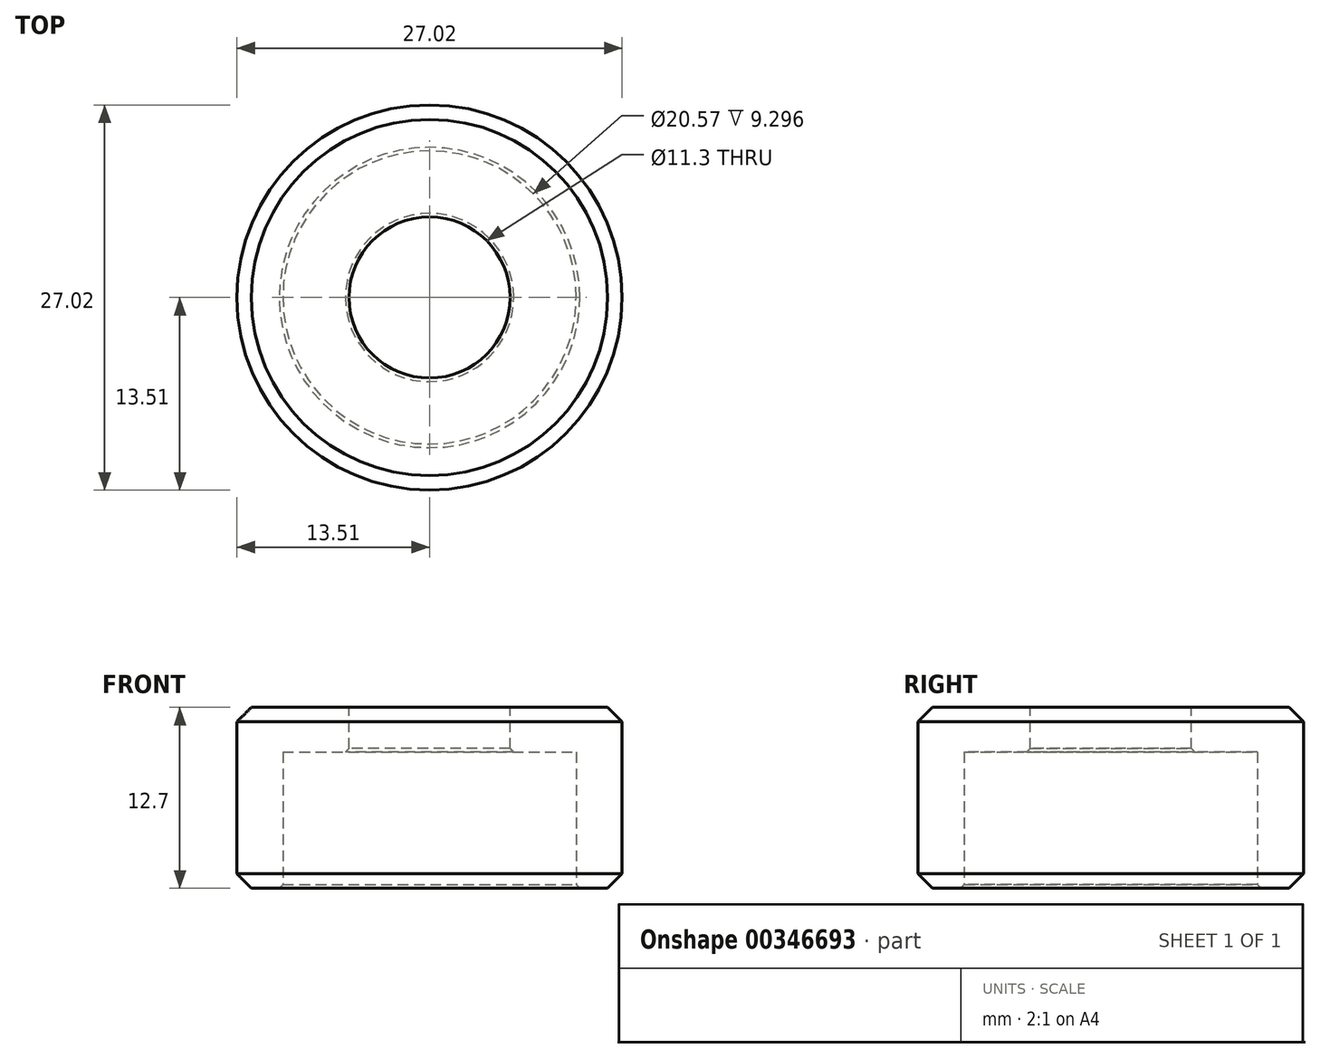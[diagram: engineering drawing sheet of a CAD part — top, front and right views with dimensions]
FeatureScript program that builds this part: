
annotation { "Feature Type Name" : "Feature", "Feature Type Description" : "" }
export const myFeature = defineFeature(function(context is Context, id is Id, definition is map)
    precondition{}
    {
        {
            var Q0;
            Q0=qCreatedBy(makeId("Front.planeOp"),FACE);
            var sketch = newSketch(context, id + "F0", { "sketchPlane" : qUnion([Q0])});
            skLineSegment(sketch, "E0.bottom", {"start": v(0, 0) * mm, "end": v(13.51, 0) * mm});
            skLineSegment(sketch, "E0.top", {"start": v(0, 12.7) * mm, "end": v(13.51, 12.7) * mm});
            skLineSegment(sketch, "E0.left", {"start": v(0, 0) * mm, "end": v(0, 12.7) * mm});
            skLineSegment(sketch, "E0.right", {"start": v(13.51, 0) * mm, "end": v(13.51, 12.7) * mm});
            skLineSegment(sketch, "E1", {"start": v(13.51, 0) * mm, "end": v(10.29, 0) * mm});
            skLineSegment(sketch, "E2", {"start": v(10.29, 0) * mm, "end": v(10.29, 9.55) * mm});
            skLineSegment(sketch, "E3", {"start": v(10.29, 9.55) * mm, "end": v(0, 9.55) * mm});
            skSolve(sketch);
        }
        {
            var Q0;
            {var subQ1=sQuery(id+"F0.wireOp",EDGE,"E0.top");Q0=makeQuery(id+"F0.imprint","IMPRINT",FACE,{"disambiguationData":[TD([[makeQuery(id+"F0.imprint","IMPRINT",EDGE,{"derivedFrom":subQ1}),-1.0]])]});}
            var Q1;
            Q1=sQuery(id+"F0.wireOp",EDGE,"E0.left");
            revolve(context, id + "F1", {"entities" : qUnion([Q0]), "axis" : qUnion([Q1]), "revolveType" : RevolveType.FULL});
        }
        {
            var Q0;
            Q0=makeQuery(id+"F1.opRevolve","SWEPT_EDGE",EDGE,{"disambiguationData":[OSD([sQuery(id+"F0.wireOp",EDGE,"E0.top"),sQuery(id+"F0.wireOp",EDGE,"E0.right")])]});
            var Q1;
            Q1=makeQuery(id+"F1.opRevolve","SWEPT_EDGE",EDGE,{"disambiguationData":[OSD([sQuery(id+"F0.wireOp",EDGE,"E0.right"),sQuery(id+"F0.wireOp",EDGE,"E1")])]});
            chamfer(context, id + "F2", {"entities" : qUnion([Q0, Q1]), "width" : 1.02 * mm, "tangentPropagation" : true});
        }
        {
            var Q0;
            Q0=makeQuery(id+"F1.opRevolve","SWEPT_FACE",FACE,{"disambiguationData":[OSD([sQuery(id+"F0.wireOp",EDGE,"E0.top")])]});
            var sketch = newSketch(context, id + "F3", { "sketchPlane" : qUnion([Q0])});
            skCircle(sketch, "E4", {"center": v(0, 0) * mm, "radius": 5.65 * mm});
            skSolve(sketch);
        }
        {
            var Q0;
            Q0 = qSketchRegion(id + "F3", true);
            extrude(context, id + "F4", {"entities" : qUnion([Q0]), "operationType" : NewBodyOperationType.REMOVE, "oppositeDirection" : true, "depth" : 25.4 * mm});
        }
        {
            var Q0;
            Q0=makeQuery(id+"F4.boolean.opBoolean","COPY",EDGE,{"derivedFrom":makeQuery(id+"F4.opExtrude","CAP_EDGE",EDGE,{"disambiguationData":[OSD([sQuery(id+"F3.wireOp",EDGE,"E4")])],"isStart":true})});
            var Q1;
            Q1=makeQuery(id+"F4.boolean.opBoolean","INTERSECT",EDGE,{"derivedFrom":[makeQuery(id+"F1.opRevolve","SWEPT_FACE",FACE,{"disambiguationData":[OSD([sQuery(id+"F0.wireOp",EDGE,"E3")])]}),makeQuery(id+"F4.opExtrude","SWEPT_FACE",FACE,{"disambiguationData":[OSD([sQuery(id+"F3.wireOp",EDGE,"E4")])]})]});
            var Q2;
            Q2=makeQuery(id+"F1.opRevolve","SWEPT_EDGE",EDGE,{"disambiguationData":[OSD([sQuery(id+"F0.wireOp",EDGE,"E0.bottom"),sQuery(id+"F0.wireOp",EDGE,"E1"),sQuery(id+"F0.wireOp",EDGE,"E2")])]});
            chamfer(context, id + "F5", {"entities" : qUnion([Q0, Q1, Q2]), "width" : 0.25 * mm, "tangentPropagation" : true});
        }
    });
